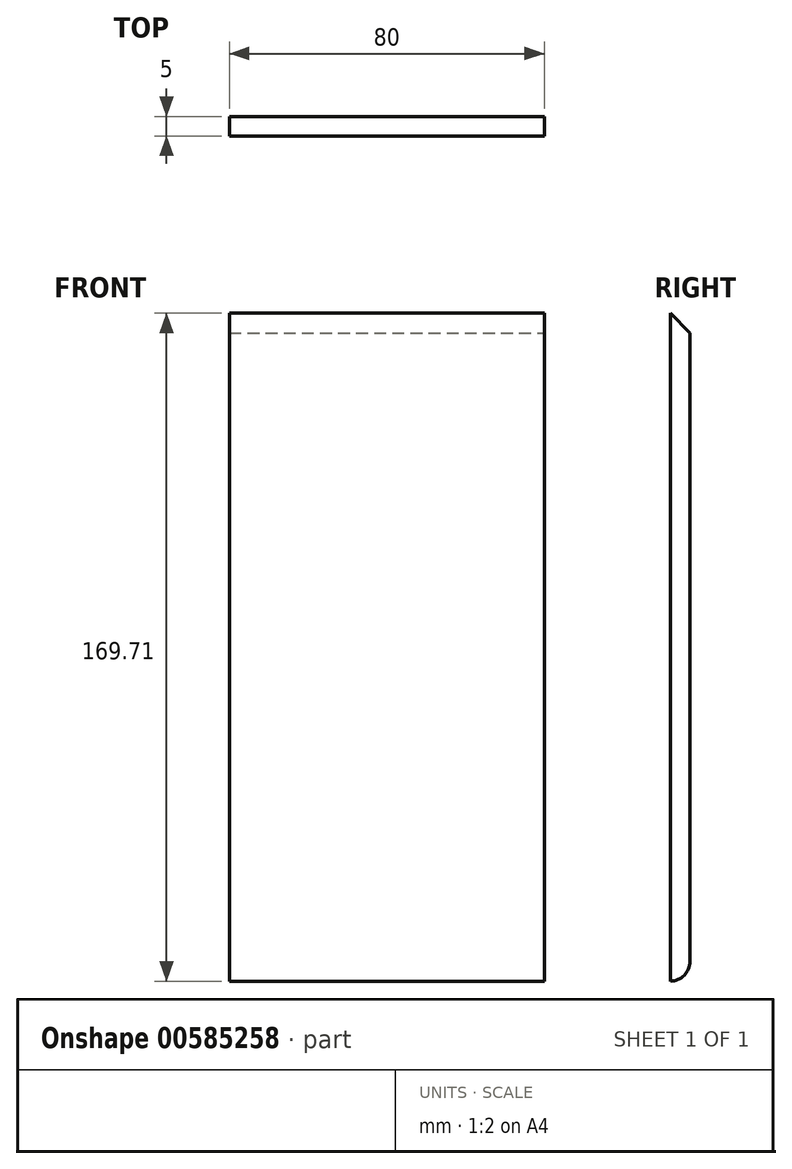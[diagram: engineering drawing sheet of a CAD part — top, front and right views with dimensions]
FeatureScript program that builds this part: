
annotation { "Feature Type Name" : "Feature", "Feature Type Description" : "" }
export const myFeature = defineFeature(function(context is Context, id is Id, definition is map)
    precondition{}
    {
        {
            var Q0;
            Q0=qCreatedBy(makeId("Front.planeOp"),FACE);
            var sketch = newSketch(context, id + "F0", { "sketchPlane" : qUnion([Q0])});
            skLineSegment(sketch, "E0", {"start": v(-77.08, -64.3) * mm, "end": v(2.92, -64.3) * mm});
            skLineSegment(sketch, "E1", {"start": v(-77.08, 105.41) * mm, "end": v(2.92, 105.41) * mm});
            skLineSegment(sketch, "E2", {"start": v(-77.08, 105.41) * mm, "end": v(-77.08, -64.3) * mm});
            skLineSegment(sketch, "E3", {"start": v(2.92, 105.41) * mm, "end": v(2.92, -64.3) * mm});
            skSolve(sketch);
        }
        {
            var Q0;
            Q0 = qSketchRegion(id + "F0", true);
            extrude(context, id + "F1", {"entities" : qUnion([Q0]), "depth" : 5 * mm, "offsetDistance" : 25 * mm});
        }
        {
            var Q0;
            Q0=makeQuery(id+"F1.opExtrude","CAP_EDGE",EDGE,{"disambiguationData":[OSD([sQuery(id+"F0.wireOp",EDGE,"E1")])],"isStart":true});
            chamfer(context, id + "F2", {"entities" : qUnion([Q0]), "width" : 5 * mm, "tangentPropagation" : true});
        }
        {
            var Q0;
            Q0=makeQuery(id+"F1.opExtrude","CAP_EDGE",EDGE,{"disambiguationData":[OSD([sQuery(id+"F0.wireOp",EDGE,"E0")])],"isStart":true});
            fillet(context, id + "F3", {"entities" : qUnion([Q0]), "radius" : 5 * mm, "tangentPropagation" : true, "allowEdgeOverflow" : false});
        }
    });
